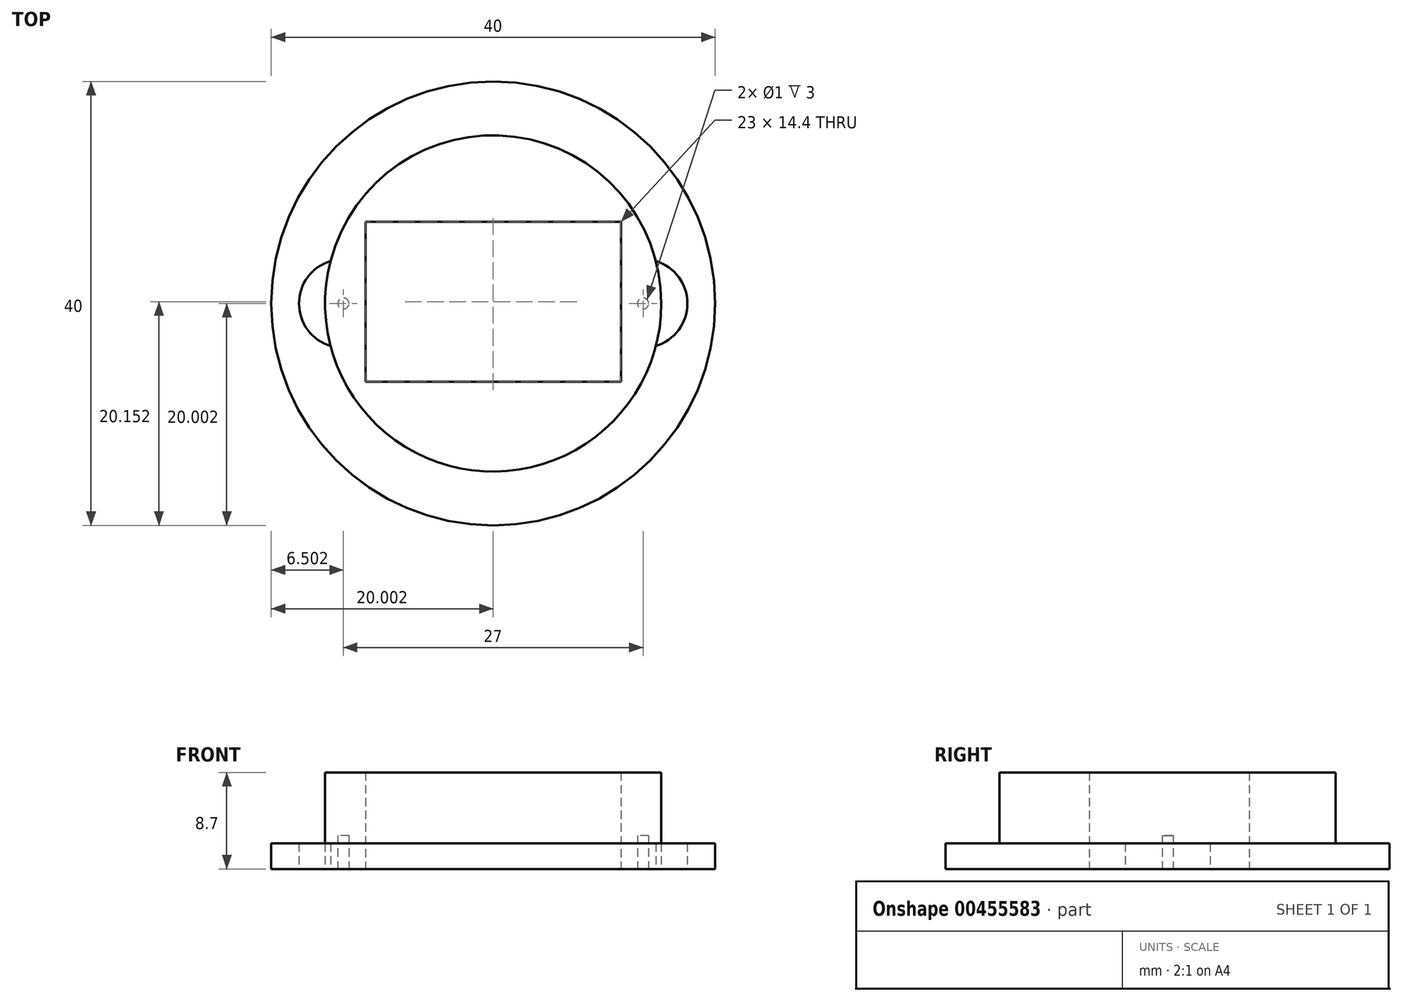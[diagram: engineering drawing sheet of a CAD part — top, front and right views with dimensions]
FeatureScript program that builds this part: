
annotation { "Feature Type Name" : "Feature", "Feature Type Description" : "" }
export const myFeature = defineFeature(function(context is Context, id is Id, definition is map)
    precondition{}
    {
        {
            var Q0;
            Q0=qCreatedBy(makeId("Top.planeOp"),FACE);
            var sketch = newSketch(context, id + "F0", { "sketchPlane" : qUnion([Q0])});
            skLineSegment(sketch, "E0.bottom", {"start": v(-52.23, 32.32) * mm, "end": v(-29.23, 32.32) * mm});
            skLineSegment(sketch, "E0.top", {"start": v(-52.23, 17.92) * mm, "end": v(-29.23, 17.92) * mm});
            skLineSegment(sketch, "E0.left", {"start": v(-52.23, 32.32) * mm, "end": v(-52.23, 17.92) * mm});
            skLineSegment(sketch, "E0.right", {"start": v(-29.23, 32.32) * mm, "end": v(-29.23, 17.92) * mm});
            skLineSegment(sketch, "E1", {"start": v(-54.23, 24.97) * mm, "end": v(-27.23, 24.97) * mm});
            skLineSegment(sketch, "E2", {"start": v(-40.73, 32.32) * mm, "end": v(-40.73, 17.92) * mm, "construction": true});
            skPoint(sketch, "E3", {"position": v(-40.73, 24.97) * mm});
            skCircle(sketch, "E4", {"center": v(-54.23, 24.97) * mm, "radius": 0.5 * mm});
            skCircle(sketch, "E5", {"center": v(-27.23, 24.97) * mm, "radius": 0.5 * mm});
            skArc(sketch, "E6", {"start": v(-54.23, 20.97) * mm, "mid": v(-58.23, 24.97) * mm, "end": v(-54.23, 28.97) * mm});
            skLineSegment(sketch, "E7", {"start": v(-54.23, 28.97) * mm, "end": v(-52.23, 28.97) * mm});
            skLineSegment(sketch, "E8", {"start": v(-54.23, 20.97) * mm, "end": v(-52.23, 20.97) * mm});
            skArc(sketch, "E9.MirrorCS", {"start": v(-27.23, 20.97) * mm, "mid": v(-23.23, 24.97) * mm, "end": v(-27.23, 28.97) * mm});
            skLineSegment(sketch, "E10.MirrorCS", {"start": v(-27.23, 20.97) * mm, "end": v(-29.23, 20.97) * mm});
            skLineSegment(sketch, "E11.MirrorCS", {"start": v(-27.23, 28.97) * mm, "end": v(-29.23, 28.97) * mm});
            skCircle(sketch, "E12", {"center": v(-40.73, 24.97) * mm, "radius": 15.15 * mm});
            skCircle(sketch, "E13", {"center": v(-40.73, 24.97) * mm, "radius": 20 * mm});
            skSolve(sketch);
        }
        {
            var Q0;
            Q0=makeQuery(id+"F0.imprint","IMPRINT",FACE,{"disambiguationData":[TD([[makeQuery(id+"F0.imprint","IMPRINT",EDGE,{"derivedFrom":sQuery(id+"F0.wireOp",EDGE,"E4")}),-1.0]])]});
            var Q1;
            Q1=makeQuery(id+"F0.imprint","IMPRINT",FACE,{"disambiguationData":[TD([[makeQuery(id+"F0.imprint","IMPRINT",EDGE,{"derivedFrom":sQuery(id+"F0.wireOp",EDGE,"E4")}),1.0]])]});
            var Q2;
            Q2=makeQuery(id+"F0.imprint","IMPRINT",FACE,{"disambiguationData":[TD([[makeQuery(id+"F0.imprint","IMPRINT",EDGE,{"derivedFrom":sQuery(id+"F0.wireOp",EDGE,"E5")}),-1.0]])]});
            var Q3;
            Q3=makeQuery(id+"F0.imprint","IMPRINT",FACE,{"disambiguationData":[TD([[makeQuery(id+"F0.imprint","IMPRINT",EDGE,{"derivedFrom":sQuery(id+"F0.wireOp",EDGE,"E5")}),1.0]])]});
            var Q4;
            {var subQ5=sQuery(id+"F0.wireOp",EDGE,"E0.top");Q4=makeQuery(id+"F0.imprint","IMPRINT",FACE,{"disambiguationData":[TD([[makeQuery(id+"F0.imprint","IMPRINT",EDGE,{"derivedFrom":subQ5}),-1.0]])]});}
            var Q5;
            {var subQ1=sQuery(id+"F0.wireOp",EDGE,"E0.bottom");Q5=makeQuery(id+"F0.imprint","IMPRINT",FACE,{"disambiguationData":[TD([[makeQuery(id+"F0.imprint","IMPRINT",EDGE,{"derivedFrom":subQ1}),1.0]])]});}
            extrude(context, id + "F1", {"entities" : qUnion([Q0, Q1, Q2, Q3, Q4, Q5]), "depth" : 8.7 * mm, "offsetDistance" : 25 * mm});
        }
        {
            var Q0;
            Q0=makeQuery(id+"F0.imprint","IMPRINT",FACE,{"disambiguationData":[TD([[makeQuery(id+"F0.imprint","IMPRINT",EDGE,{"derivedFrom":sQuery(id+"F0.wireOp",EDGE,"E12")}),-1.0]])]});
            var Q1;
            {var subQ0=sQuery(id+"F0.wireOp",EDGE,"E12");var subQ1=sQuery(id+"F0.wireOp",EDGE,"E6");var subQ2=makeQuery(id+"F0.imprint","INTERSECT",VERTEX,{"disambiguationData":[OD(0.0)],"derivedFrom":[subQ1,subQ0]});Q1=makeQuery(id+"F0.imprint","IMPRINT",FACE,{"disambiguationData":[TD([[makeQuery(id+"F0.imprint","IMPRINT",EDGE,{"disambiguationData":[TD([[subQ2,-1.0]])],"derivedFrom":subQ1}),-1.0]])]});}
            var Q2;
            {var subQ0=sQuery(id+"F0.wireOp",EDGE,"E12");var subQ1=sQuery(id+"F0.wireOp",EDGE,"E9.MirrorCS");var subQ2=makeQuery(id+"F0.imprint","INTERSECT",VERTEX,{"disambiguationData":[OD(0.0)],"derivedFrom":[subQ1,subQ0]});Q2=makeQuery(id+"F0.imprint","IMPRINT",FACE,{"disambiguationData":[TD([[makeQuery(id+"F0.imprint","IMPRINT",EDGE,{"disambiguationData":[TD([[subQ2,-1.0]])],"derivedFrom":subQ1}),1.0]])]});}
            extrude(context, id + "F2", {"entities" : qUnion([Q0, Q1, Q2]), "operationType" : NewBodyOperationType.ADD, "depth" : 2.3 * mm, "offsetDistance" : 25 * mm});
        }
        {
            var Q0;
            Q0=makeQuery(id+"F0.imprint","IMPRINT",FACE,{"disambiguationData":[TD([[makeQuery(id+"F0.imprint","IMPRINT",EDGE,{"derivedFrom":sQuery(id+"F0.wireOp",EDGE,"E4")}),1.0]])]});
            var Q1;
            Q1=makeQuery(id+"F0.imprint","IMPRINT",FACE,{"disambiguationData":[TD([[makeQuery(id+"F0.imprint","IMPRINT",EDGE,{"derivedFrom":sQuery(id+"F0.wireOp",EDGE,"E5")}),1.0]])]});
            extrude(context, id + "F3", {"entities" : qUnion([Q0, Q1]), "operationType" : NewBodyOperationType.REMOVE, "depth" : 3 * mm, "offsetDistance" : 25 * mm});
        }
    });
